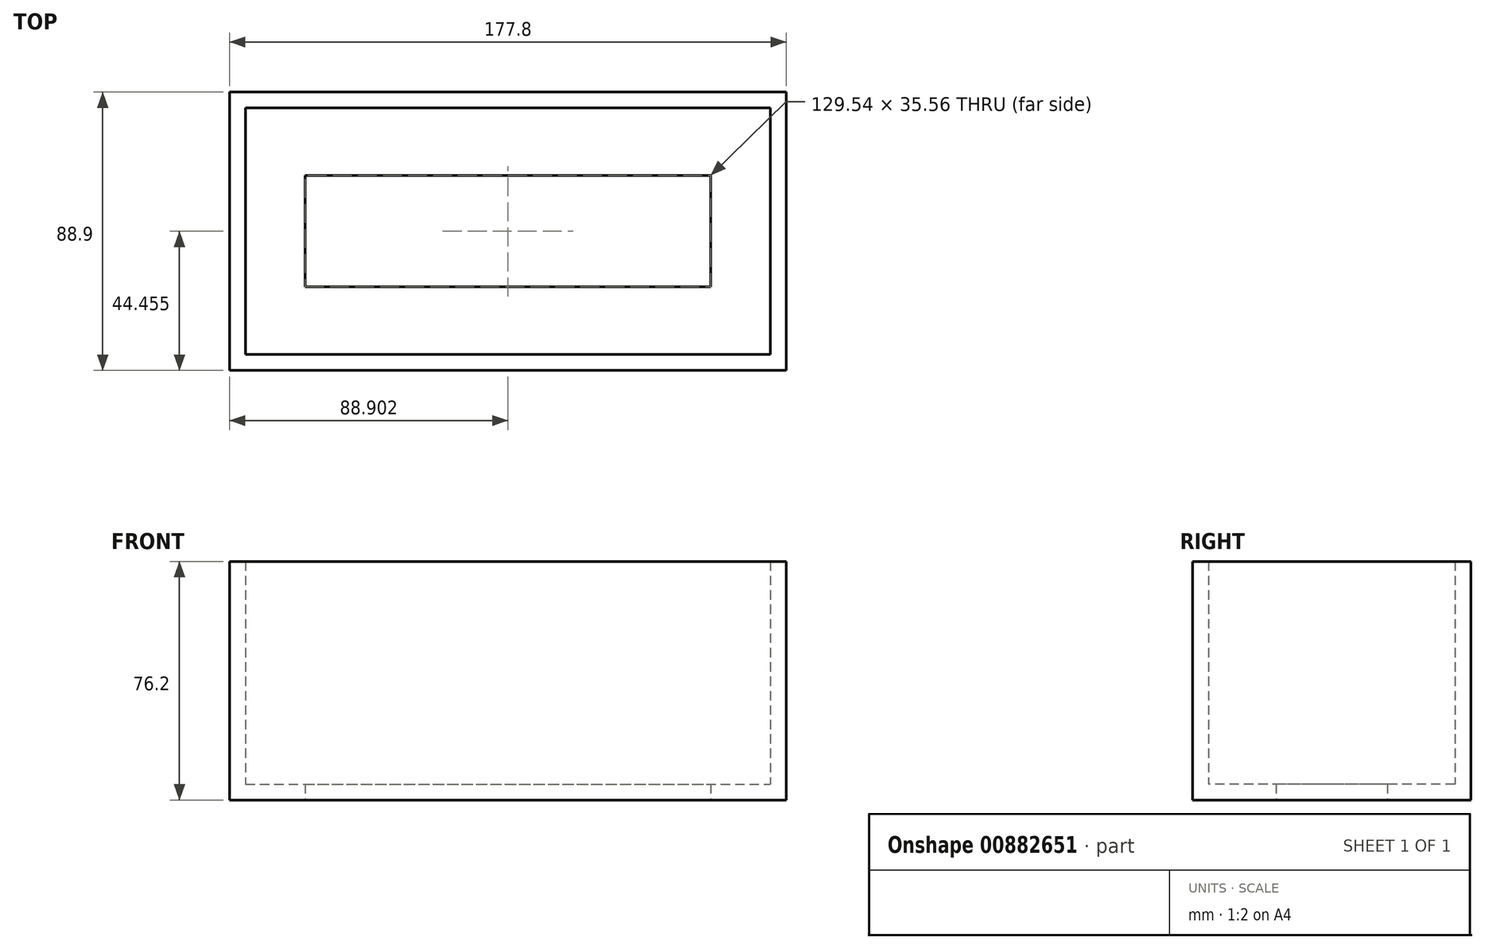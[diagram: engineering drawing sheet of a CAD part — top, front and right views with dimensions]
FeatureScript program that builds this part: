
annotation { "Feature Type Name" : "Feature", "Feature Type Description" : "" }
export const myFeature = defineFeature(function(context is Context, id is Id, definition is map)
    precondition{}
    {
        {
            var Q0;
            Q0=qCreatedBy(makeId("Top.planeOp"),FACE);
            var sketch = newSketch(context, id + "F0", { "sketchPlane" : qUnion([Q0])});
            skLineSegment(sketch, "E0.bottom", {"start": v(-33.77, 8.67) * mm, "end": v(95.77, 8.67) * mm});
            skLineSegment(sketch, "E0.top", {"start": v(-33.77, -26.89) * mm, "end": v(95.77, -26.89) * mm});
            skLineSegment(sketch, "E0.left", {"start": v(-33.77, 8.67) * mm, "end": v(-33.77, -26.89) * mm});
            skLineSegment(sketch, "E0.right", {"start": v(95.77, 8.67) * mm, "end": v(95.77, -26.89) * mm});
            skLineSegment(sketch, "E1.bottom", {"start": v(-52.82, 30.26) * mm, "end": v(114.82, 30.26) * mm});
            skLineSegment(sketch, "E1.top", {"start": v(-52.82, -48.48) * mm, "end": v(114.82, -48.48) * mm});
            skLineSegment(sketch, "E1.left", {"start": v(-52.82, 30.26) * mm, "end": v(-52.82, -48.48) * mm});
            skLineSegment(sketch, "E1.right", {"start": v(114.82, 30.26) * mm, "end": v(114.82, -48.48) * mm});
            skLineSegment(sketch, "E2.bottom", {"start": v(-57.9, 35.34) * mm, "end": v(119.9, 35.34) * mm});
            skLineSegment(sketch, "E2.top", {"start": v(-57.9, -53.56) * mm, "end": v(119.9, -53.56) * mm});
            skLineSegment(sketch, "E2.left", {"start": v(-57.9, 35.34) * mm, "end": v(-57.9, -53.56) * mm});
            skLineSegment(sketch, "E2.right", {"start": v(119.9, 35.34) * mm, "end": v(119.9, -53.56) * mm});
            skSolve(sketch);
        }
        {
            var Q0;
            Q0=makeQuery(id+"F0.imprint","IMPRINT",FACE,{"disambiguationData":[TD([[makeQuery(id+"F0.imprint","IMPRINT",EDGE,{"derivedFrom":sQuery(id+"F0.wireOp",EDGE,"E1.bottom")}),1.0]])]});
            extrude(context, id + "F1", {"entities" : qUnion([Q0]), "depth" : 76.2 * mm, "offsetDistance" : 25.4 * mm});
        }
        {
            var Q0;
            Q0 = qSketchRegion(id + "F0", true);
            var Q1;
            Q1=makeQuery(id+"F0.imprint","IMPRINT",FACE,{"disambiguationData":[TD([[makeQuery(id+"F0.imprint","IMPRINT",EDGE,{"derivedFrom":sQuery(id+"F0.wireOp",EDGE,"E0.bottom")}),1.0]])]});
            extrude(context, id + "F2", {"entities" : qUnion([Q0, Q1]), "operationType" : NewBodyOperationType.ADD, "depth" : 5.08 * mm, "offsetDistance" : 25.4 * mm});
        }
    });
